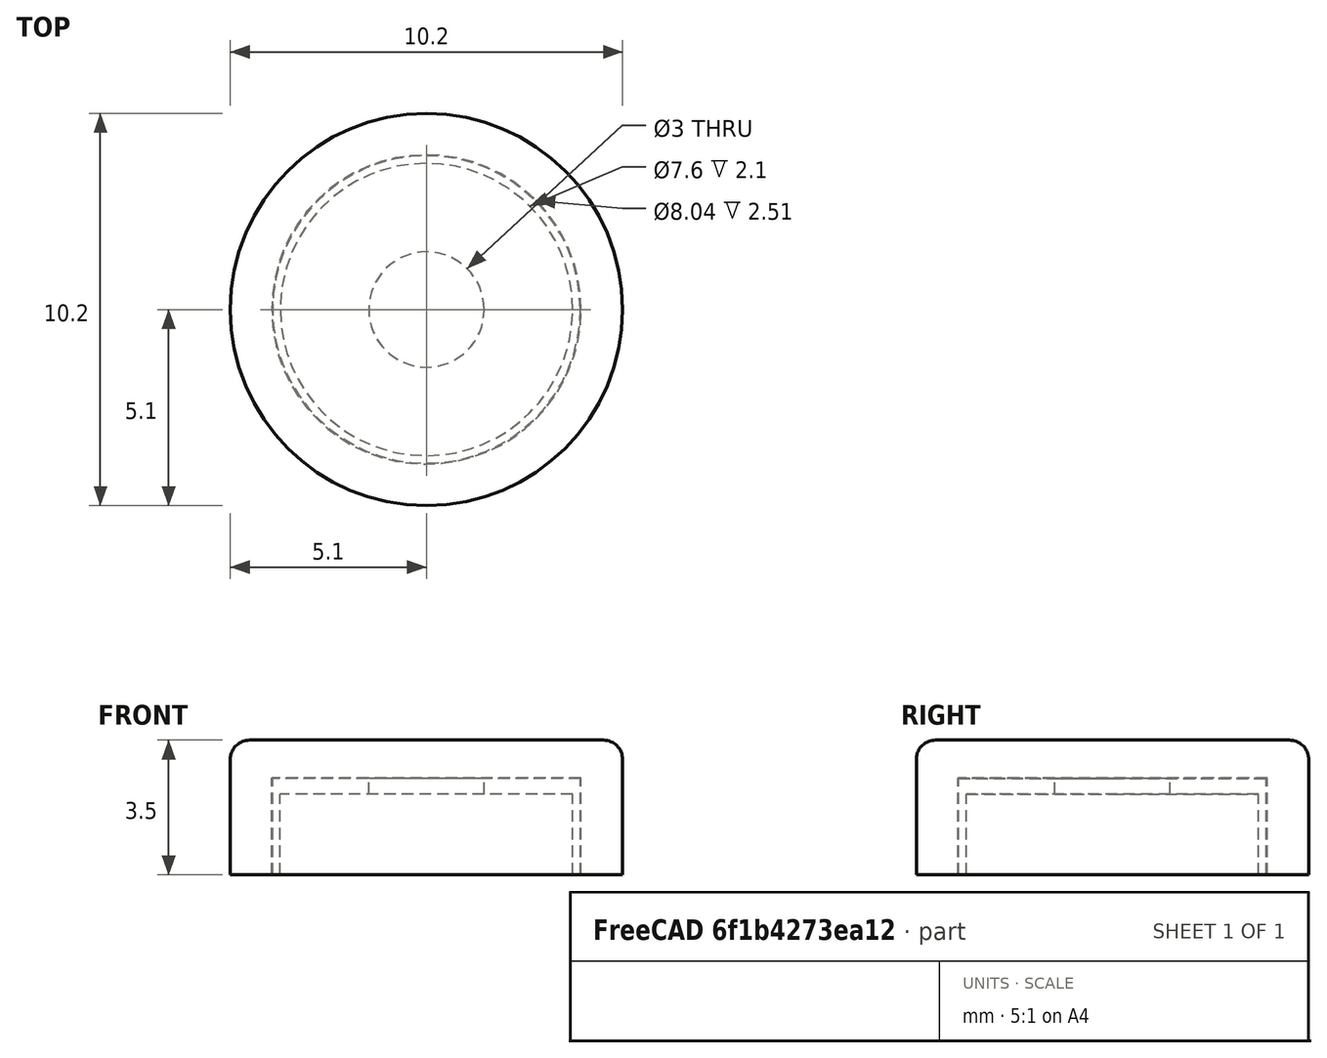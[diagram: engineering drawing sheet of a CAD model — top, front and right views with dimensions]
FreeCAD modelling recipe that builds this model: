
FCSTD DOCUMENT  (FreeCAD 0.17R13541 (Git))
Label: E-Switch_TL3240R1CAPBLK
License: All rights reserved
LicenseURL: http://en.wikipedia.org/wiki/All_rights_reserved
objects: Part::Cylinder×5, Part::Cut×2, Part::Fillet×1, Part::Fuse×1, App::Part×1
note: 9 computed .brp shape members not serialized (recipe doc carries the construction recipe); baked Part::Feature solids carry a one-line shape summary decoded from their .brp

FEATURE [Part::Cylinder] Cylinder
  Angle = 360
  AttacherType = Attacher::AttachEngine3D
  Height = 3.5
  Radius = 5.1
FEATURE [Part::Cylinder] Cylinder001
  Angle = 360
  AttacherType = Attacher::AttachEngine3D
  Height = 2.51
  Radius = 4.02
FEATURE [Part::Cut] Cut
  Base = -> Cylinder
  Tool = -> Cylinder001
FEATURE [Part::Fillet] Fillet
  Base = -> Cut
  Edges = 1 edges r=0.5: [Edge1]
FEATURE [Part::Cylinder] Cylinder002
  Angle = 360
  AttacherType = Attacher::AttachEngine3D
  Height = 2.5
  Radius = 4
FEATURE [Part::Cylinder] Cylinder003
  Angle = 360
  AttacherType = Attacher::AttachEngine3D
  Height = 2.1
  Radius = 3.8
FEATURE [Part::Cylinder] Cylinder004
  Angle = 360
  AttacherType = Attacher::AttachEngine3D
  Height = 3
  Radius = 1.5
FEATURE [Part::Fuse] Fusion
  Base = -> Cylinder003
  Tool = -> Cylinder004
FEATURE [Part::Cut] Cut001
  Base = -> Cylinder002
  Tool = -> Fusion
FEATURE [App::Part] Part
  Group = -> [Cylinder001,Cylinder,Cut,Fillet,Cylinder002,Fusion,Cylinder004,Cylinder003,Cut001]
  License = CC BY 3.0
  LicenseURL = http://creativecommons.org/licenses/by/3.0/
  Origin = -> Origin
